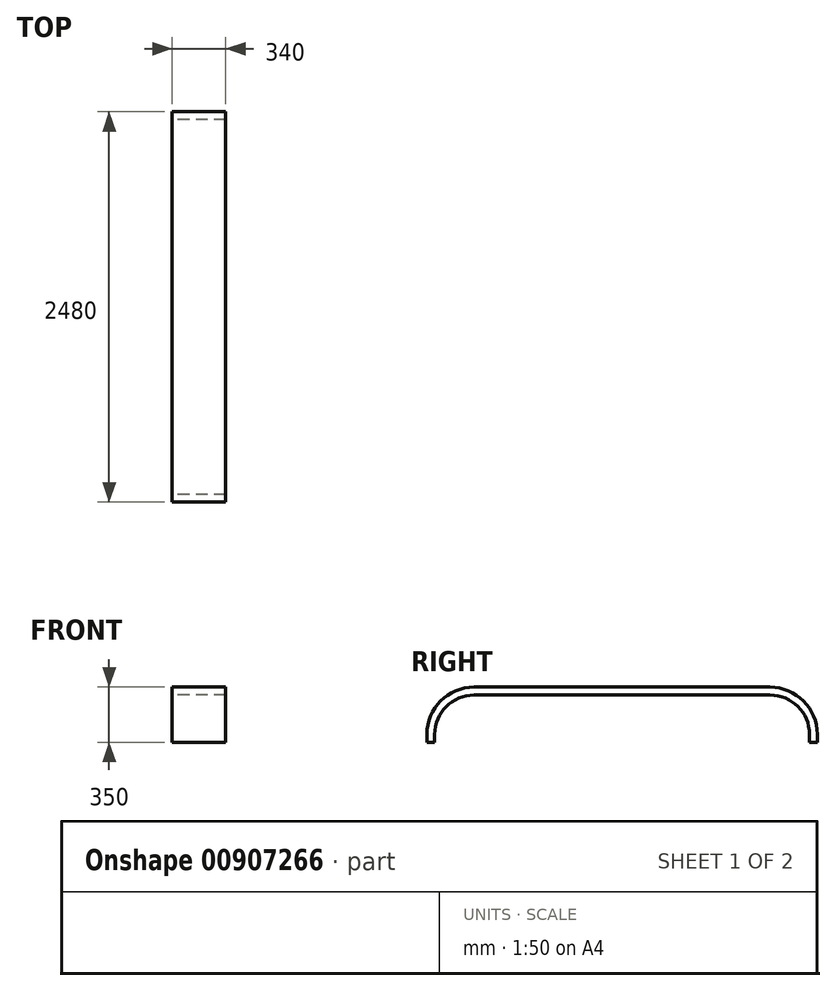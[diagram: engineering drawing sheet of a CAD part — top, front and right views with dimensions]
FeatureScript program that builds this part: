
annotation { "Feature Type Name" : "Feature", "Feature Type Description" : "" }
export const myFeature = defineFeature(function(context is Context, id is Id, definition is map)
    precondition{}
    {
        {
            var Q0;
            Q0=qCreatedBy(makeId("Right.planeOp"),FACE);
            var sketch = newSketch(context, id + "F0", { "sketchPlane" : qUnion([Q0])});
            skLineSegment(sketch, "E0.bottom", {"start": v(0, 0) * mm, "end": v(50, 0) * mm});
            skLineSegment(sketch, "E0.top", {"start": v(300, 350) * mm, "end": v(2180, 350) * mm});
            skLineSegment(sketch, "E0.left", {"start": v(0, 0) * mm, "end": v(0, 50) * mm});
            skLineSegment(sketch, "E0.right", {"start": v(2480, 0) * mm, "end": v(2480, 50) * mm});
            skPoint(sketch, "E1.visualSharp", {"position": v(0, 350) * mm});
            skArc(sketch, "E1.filletArc", {"start": v(300, 350) * mm, "mid": v(87.87, 262.13) * mm, "end": v(0, 50) * mm});
            skPoint(sketch, "E2.visualSharp", {"position": v(2480, 350) * mm});
            skArc(sketch, "E2.filletArc", {"start": v(2480, 50) * mm, "mid": v(2392.13, 262.13) * mm, "end": v(2180, 350) * mm});
            skArc(sketch, "E3.0", {"start": v(300, 300) * mm, "mid": v(123.22, 226.78) * mm, "end": v(50, 50) * mm});
            skArc(sketch, "E3.1", {"start": v(2430, 50) * mm, "mid": v(2356.78, 226.78) * mm, "end": v(2180, 300) * mm});
            skLineSegment(sketch, "E3.2", {"start": v(2430, 50) * mm, "end": v(2430, 50) * mm});
            skLineSegment(sketch, "E3.3", {"start": v(300, 300) * mm, "end": v(2180, 300) * mm});
            skLineSegment(sketch, "E3.5", {"start": v(50, 50) * mm, "end": v(50, 50) * mm});
            skLineSegment(sketch, "E4", {"start": v(50, 50) * mm, "end": v(50, 0) * mm});
            skLineSegment(sketch, "E5", {"start": v(2430, 50) * mm, "end": v(2430, 0) * mm});
            skLineSegment(sketch, "E6", {"start": v(2430, 0) * mm, "end": v(2480, 0) * mm});
            skSolve(sketch);
        }
        {
            var Q0;
            Q0=makeQuery(id+"F0.imprint","IMPRINT",FACE,{"disambiguationData":[TD([[makeQuery(id+"F0.imprint","IMPRINT",EDGE,{"derivedFrom":sQuery(id+"F0.wireOp",EDGE,"E0.bottom")}),1.0]])]});
            extrude(context, id + "F1", {"entities" : qUnion([Q0]), "endBound" : BoundingType.SYMMETRIC, "depth" : 340 * mm, "offsetDistance" : 25 * mm});
        }
    });
